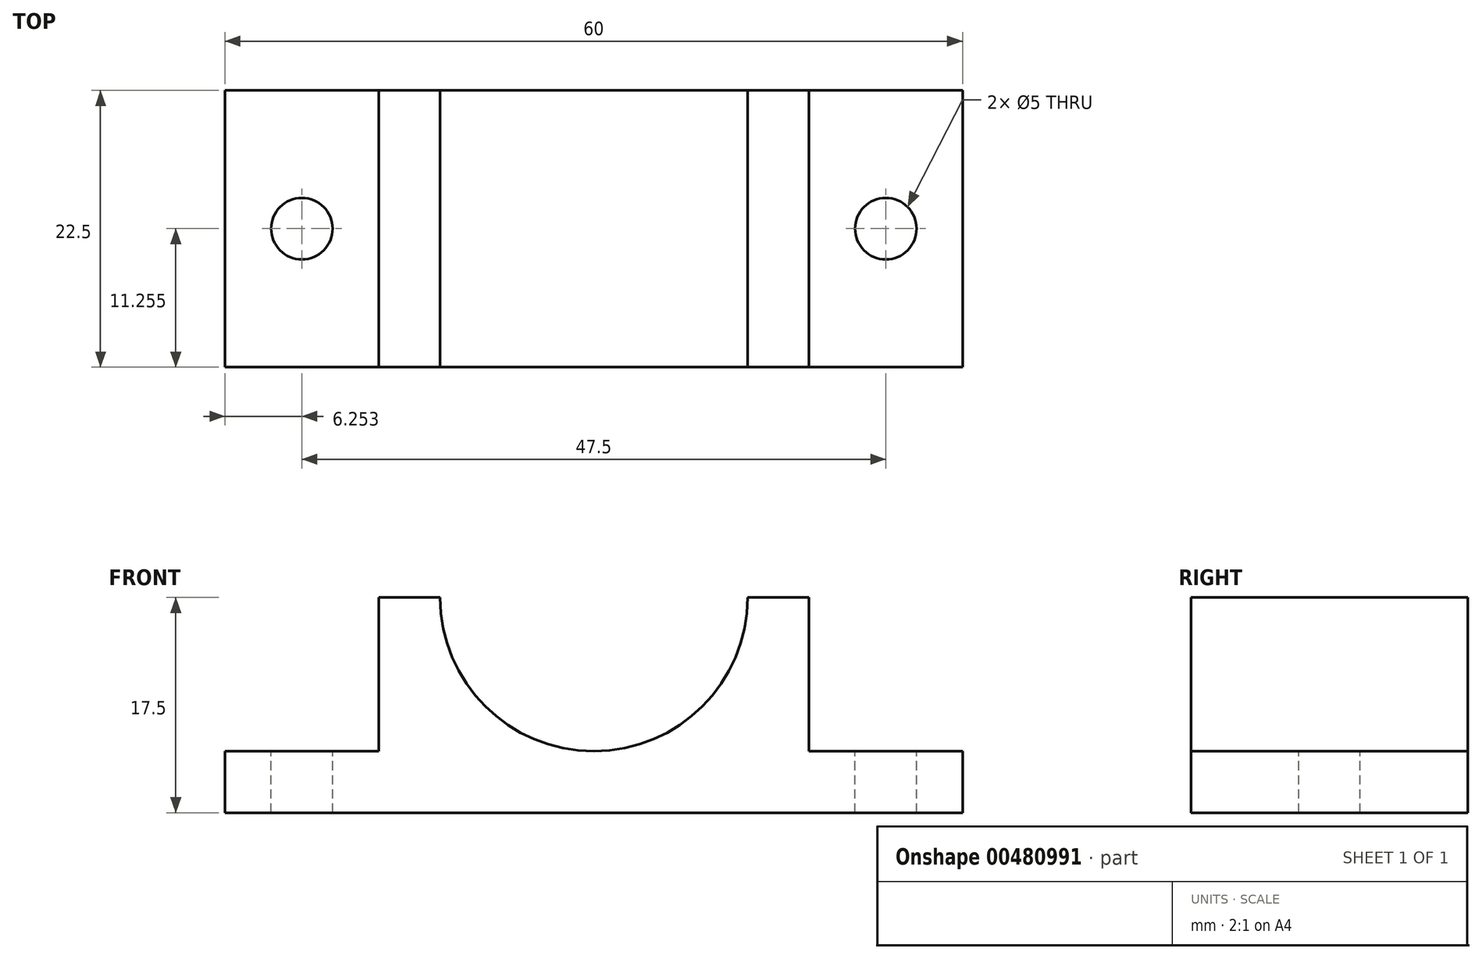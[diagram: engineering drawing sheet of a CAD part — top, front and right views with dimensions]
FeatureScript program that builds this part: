
annotation { "Feature Type Name" : "Feature", "Feature Type Description" : "" }
export const myFeature = defineFeature(function(context is Context, id is Id, definition is map)
    precondition{}
    {
        {
            var Q0;
            Q0=qCreatedBy(makeId("Top.planeOp"),FACE);
            var sketch = newSketch(context, id + "F0", { "sketchPlane" : qUnion([Q0])});
            skLineSegment(sketch, "E0.bottom", {"start": v(-9.48, 5.56) * mm, "end": v(50.52, 5.56) * mm});
            skLineSegment(sketch, "E0.top", {"start": v(-9.48, -16.94) * mm, "end": v(50.52, -16.94) * mm});
            skLineSegment(sketch, "E0.left", {"start": v(-9.48, 5.56) * mm, "end": v(-9.48, -16.94) * mm});
            skLineSegment(sketch, "E0.right", {"start": v(50.52, 5.56) * mm, "end": v(50.52, -16.94) * mm});
            skSolve(sketch);
        }
        {
            var Q0;
            Q0=makeQuery(id+"F0.imprint","IMPRINT",FACE,{"disambiguationData":[TD([[makeQuery(id+"F0.imprint","IMPRINT",EDGE,{"derivedFrom":sQuery(id+"F0.wireOp",EDGE,"E0.bottom")}),-1.0]])]});
            extrude(context, id + "F1", {"entities" : qUnion([Q0]), "depth" : 5 * mm});
        }
        {
            var Q0;
            Q0=makeQuery(id+"F1.opExtrude","CAP_FACE",FACE,{"disambiguationData":[OSD([sQuery(id+"F0.wireOp",EDGE,"E0.bottom"),sQuery(id+"F0.wireOp",EDGE,"E0.top"),sQuery(id+"F0.wireOp",EDGE,"E0.left"),sQuery(id+"F0.wireOp",EDGE,"E0.right")])],"isStart":false});
            var sketch = newSketch(context, id + "F2", { "sketchPlane" : qUnion([Q0])});
            skLineSegment(sketch, "E1.bottom", {"start": v(50.52, 5.56) * mm, "end": v(38.02, 5.56) * mm});
            skLineSegment(sketch, "E1.top", {"start": v(50.52, -16.94) * mm, "end": v(38.02, -16.94) * mm});
            skLineSegment(sketch, "E1.left", {"start": v(50.52, 5.56) * mm, "end": v(50.52, -16.94) * mm});
            skLineSegment(sketch, "E1.right", {"start": v(38.02, 5.56) * mm, "end": v(38.02, -16.94) * mm});
            skLineSegment(sketch, "E2.bottom", {"start": v(-9.48, 5.56) * mm, "end": v(3.02, 5.56) * mm});
            skLineSegment(sketch, "E2.top", {"start": v(-9.48, -16.94) * mm, "end": v(3.02, -16.94) * mm});
            skLineSegment(sketch, "E2.left", {"start": v(-9.48, 5.56) * mm, "end": v(-9.48, -16.94) * mm});
            skLineSegment(sketch, "E2.right", {"start": v(3.02, 5.56) * mm, "end": v(3.02, -16.94) * mm});
            skSolve(sketch);
        }
        {
            var Q0;
            {var subQ0=sQuery(id+"F2.wireOp",EDGE,"E1.right");Q0=makeQuery(id+"F2.imprint","IMPRINT",FACE,{"disambiguationData":[TD([[makeQuery(id+"F2.imprint","IMPRINT",EDGE,{"derivedFrom":subQ0}),-1.0]])]});}
            extrude(context, id + "F3", {"entities" : qUnion([Q0]), "operationType" : NewBodyOperationType.ADD, "depth" : 12.5 * mm});
        }
        {
            var Q0;
            {var subQ0=sQuery(id+"F0.wireOp",EDGE,"E0.top");Q0=makeQuery(id+"F3.boolean.opBoolean","MERGE",FACE,{"derivedFrom":[makeQuery(id+"F1.opExtrude","SWEPT_FACE",FACE,{"disambiguationData":[OSD([subQ0])]}),makeQuery(id+"F3.opExtrude","SWEPT_FACE",FACE,{"disambiguationData":[OSD([subQ0])]})]});}
            var sketch = newSketch(context, id + "F4", { "sketchPlane" : qUnion([Q0])});
            skCircle(sketch, "E3", {"center": v(20.52, 17.5) * mm, "radius": 12.5 * mm});
            skSolve(sketch);
        }
        {
            var Q0;
            {var subQ0=sQuery(id+"F4.wireOp",EDGE,"E3");var subQ1=makeQuery(id+"F3.opExtrude","CAP_EDGE",EDGE,{"disambiguationData":[OSD([sQuery(id+"F0.wireOp",EDGE,"E0.top")])],"isStart":false});var subQ2=makeQuery(id+"F4.imprint","INTERSECT",VERTEX,{"disambiguationData":[OD(0.0)],"derivedFrom":[subQ1,subQ0]});Q0=makeQuery(id+"F4.imprint","IMPRINT",FACE,{"disambiguationData":[TD([[makeQuery(id+"F4.imprint","IMPRINT",EDGE,{"disambiguationData":[TD([[subQ2,1.0]])],"derivedFrom":subQ0}),1.0]])]});}
            extrude(context, id + "F5", {"entities" : qUnion([Q0]), "operationType" : NewBodyOperationType.REMOVE, "endBound" : BoundingType.THROUGH_ALL, "oppositeDirection" : true, "depth" : 25 * mm});
        }
        {
            var Q0;
            {var subQ0=sQuery(id+"F0.wireOp",EDGE,"E0.top");var subQ1=sQuery(id+"F0.wireOp",EDGE,"E0.right");var subQ2=sQuery(id+"F0.wireOp",EDGE,"E0.bottom");Q0=makeQuery(id+"F3.boolean.opBoolean","SPLIT",FACE,{"disambiguationData":[TD([makeQuery(id+"F1.opExtrude","SWEPT_FACE",FACE,{"disambiguationData":[OSD([subQ1])]})])],"derivedFrom":makeQuery(id+"F1.opExtrude","CAP_FACE",FACE,{"disambiguationData":[OSD([subQ2,subQ0,sQuery(id+"F0.wireOp",EDGE,"E0.left"),subQ1])],"isStart":false})});}
            var sketch = newSketch(context, id + "F6", { "sketchPlane" : qUnion([Q0])});
            skCircle(sketch, "E4", {"center": v(44.27, -5.69) * mm, "radius": 2.5 * mm});
            skPoint(sketch, "E4.centerSnap0", {"position": v(44.27, 5.56) * mm});
            skPoint(sketch, "E4.centerSnap1", {"position": v(50.52, -5.69) * mm});
            skSolve(sketch);
        }
        {
            var Q0;
            {var subQ0=sQuery(id+"F0.wireOp",EDGE,"E0.left");var subQ1=sQuery(id+"F0.wireOp",EDGE,"E0.top");var subQ2=sQuery(id+"F0.wireOp",EDGE,"E0.bottom");Q0=makeQuery(id+"F3.boolean.opBoolean","SPLIT",FACE,{"disambiguationData":[TD([makeQuery(id+"F1.opExtrude","SWEPT_FACE",FACE,{"disambiguationData":[OSD([subQ0])]})])],"derivedFrom":makeQuery(id+"F1.opExtrude","CAP_FACE",FACE,{"disambiguationData":[OSD([subQ2,subQ1,subQ0,sQuery(id+"F0.wireOp",EDGE,"E0.right")])],"isStart":false})});}
            var sketch = newSketch(context, id + "F7", { "sketchPlane" : qUnion([Q0])});
            skCircle(sketch, "E5", {"center": v(-3.23, -5.69) * mm, "radius": 2.5 * mm});
            skPoint(sketch, "E5.centerSnap0", {"position": v(-3.23, 5.56) * mm});
            skPoint(sketch, "E5.centerSnap1", {"position": v(-9.48, -5.69) * mm});
            skSolve(sketch);
        }
        {
            var Q0;
            Q0=makeQuery(id+"F6.imprint","IMPRINT",FACE,{"disambiguationData":[TD([[makeQuery(id+"F6.imprint","IMPRINT",EDGE,{"derivedFrom":sQuery(id+"F6.wireOp",EDGE,"E4")}),1.0]])]});
            extrude(context, id + "F8", {"entities" : qUnion([Q0]), "operationType" : NewBodyOperationType.REMOVE, "endBound" : BoundingType.THROUGH_ALL, "oppositeDirection" : true, "depth" : 25 * mm});
        }
        {
            var Q0;
            Q0=makeQuery(id+"F7.imprint","IMPRINT",FACE,{"disambiguationData":[TD([[makeQuery(id+"F7.imprint","IMPRINT",EDGE,{"derivedFrom":sQuery(id+"F7.wireOp",EDGE,"E5")}),1.0]])]});
            extrude(context, id + "F9", {"entities" : qUnion([Q0]), "operationType" : NewBodyOperationType.REMOVE, "endBound" : BoundingType.THROUGH_ALL, "oppositeDirection" : true, "depth" : 25 * mm});
        }
    });
